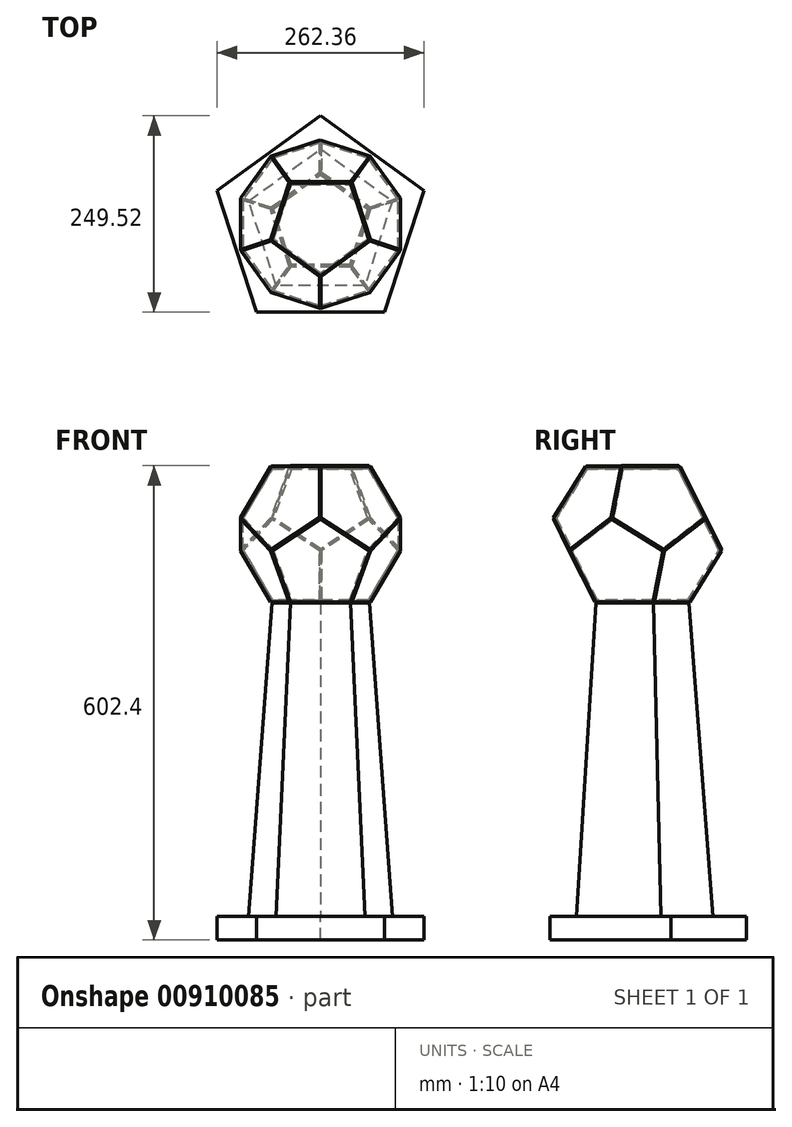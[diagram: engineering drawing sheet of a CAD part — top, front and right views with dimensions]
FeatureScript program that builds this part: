
annotation { "Feature Type Name" : "Feature", "Feature Type Description" : "" }
export const myFeature = defineFeature(function(context is Context, id is Id, definition is map)
    precondition{}
    {
        {
            var Q0;
            Q0=qCreatedBy(makeId("Top.planeOp"),FACE);
            var sketch = newSketch(context, id + "F0", { "sketchPlane" : qUnion([Q0])});
            skCircle(sketch, "E0.cCircle", {"center": v(0, 0) * mm, "radius": 52.66 * mm, "construction": true});
            skLineSegment(sketch, "E0.0", {"start": v(61.9, 20.12) * mm, "end": v(38.26, -52.66) * mm});
            skLineSegment(sketch, "E0.1", {"start": v(38.26, -52.66) * mm, "end": v(-38.26, -52.66) * mm});
            skLineSegment(sketch, "E0.2", {"start": v(-38.26, -52.66) * mm, "end": v(-61.9, 20.12) * mm});
            skLineSegment(sketch, "E0.3", {"start": v(-61.9, 20.12) * mm, "end": v(0, 65.1) * mm});
            skLineSegment(sketch, "E0.4", {"start": v(0, 65.1) * mm, "end": v(61.9, 20.12) * mm});
            skPoint(sketch, "E0.0.midPoint", {"position": v(50.09, -16.27) * mm});
            skSolve(sketch);
        }
        {
            var Q0;
            Q0=makeQuery(id+"F0.imprint","IMPRINT",FACE,{"disambiguationData":[TD([[makeQuery(id+"F0.imprint","IMPRINT",EDGE,{"derivedFrom":sQuery(id+"F0.wireOp",EDGE,"E0.0")}),-1.0]])]});
            extrude(context, id + "F1", {"entities" : qUnion([Q0]), "oppositeDirection" : true, "depth" : 2 * mm, "offsetDistance" : 25.4 * mm, "hasSecondDirection" : true, "secondDirectionOppositeDirection" : false, "secondDirectionDepth" : 2 * mm});
        }
        {
            var Q0;
            Q0=qCreatedBy(makeId("Front.planeOp"),FACE);
            var sketch = newSketch(context, id + "F2", { "sketchPlane" : qUnion([Q0])});
            skLineSegment(sketch, "E1", {"start": v(0, 0) * mm, "end": v(0, 106.17) * mm, "construction": true});
            skSolve(sketch);
        }
        {
            var Q0;
            Q0=makeQuery(id+"F1.opExtrude","SWEPT_BODY",BODY,{"disambiguationData":[OSD([sQuery(id+"F0.wireOp",EDGE,"E0.0"),sQuery(id+"F0.wireOp",EDGE,"E0.1"),sQuery(id+"F0.wireOp",EDGE,"E0.2"),sQuery(id+"F0.wireOp",EDGE,"E0.3"),sQuery(id+"F0.wireOp",EDGE,"E0.4")])]});
            transform(context, id + "F3", {"entities" : qUnion([Q0]), "transformType" : TransformType.COPY});
        }
        {
            var Q0;
            Q0=makeQuery(id+"F3.opPattern","COPY",BODY,{"derivedFrom":makeQuery(id+"F1.opExtrude","SWEPT_BODY",BODY,{"disambiguationData":[OSD([sQuery(id+"F0.wireOp",EDGE,"E0.0"),sQuery(id+"F0.wireOp",EDGE,"E0.1"),sQuery(id+"F0.wireOp",EDGE,"E0.2"),sQuery(id+"F0.wireOp",EDGE,"E0.3"),sQuery(id+"F0.wireOp",EDGE,"E0.4")])]}),"instanceName":"1"});
            var Q1;
            Q1=sQuery(id+"F0.wireOp",EDGE,"E0.4");
            transform(context, id + "F4", {"entities" : qUnion([Q0]), "transformType" : TransformType.ROTATION, "transformAxis" : qUnion([Q1]), "angle" : 116.51 * degree, "oppositeDirection" : true, "makeCopy" : false});
        }
        {
            var Q0;
            Q0=makeQuery(id+"F3.opPattern","COPY",BODY,{"derivedFrom":makeQuery(id+"F1.opExtrude","SWEPT_BODY",BODY,{"disambiguationData":[OSD([sQuery(id+"F0.wireOp",EDGE,"E0.0"),sQuery(id+"F0.wireOp",EDGE,"E0.1"),sQuery(id+"F0.wireOp",EDGE,"E0.2"),sQuery(id+"F0.wireOp",EDGE,"E0.3"),sQuery(id+"F0.wireOp",EDGE,"E0.4")])]}),"instanceName":"1"});
            var Q1;
            Q1=sQuery(id+"F2.wireOp",EDGE,"E1");
            circularPattern(context, id + "F5", {"entities" : qUnion([Q0]), "axis" : qUnion([Q1]), "angle" : 360 * degree, "instanceCount" : 5, "equalSpace" : true});
        }
        {
            var Q0;
            Q0=makeQuery(id+"F3.opPattern","COPY",FACE,{"derivedFrom":makeQuery(id+"F1.opExtrude","SWEPT_FACE",FACE,{"disambiguationData":[OSD([sQuery(id+"F0.wireOp",EDGE,"E0.1")])]}),"instanceName":"1"});
            var sketch = newSketch(context, id + "F6", { "sketchPlane" : qUnion([Q0])});
            skLineSegment(sketch, "E2", {"start": v(-23.08, 92.64) * mm, "end": v(29.66, 37.2) * mm, "construction": true});
            skSolve(sketch);
        }
        {
            var Q0;
            Q0=makeQuery(id+"F3.opPattern","COPY",BODY,{"derivedFrom":makeQuery(id+"F1.opExtrude","SWEPT_BODY",BODY,{"disambiguationData":[OSD([sQuery(id+"F0.wireOp",EDGE,"E0.0"),sQuery(id+"F0.wireOp",EDGE,"E0.1"),sQuery(id+"F0.wireOp",EDGE,"E0.2"),sQuery(id+"F0.wireOp",EDGE,"E0.3"),sQuery(id+"F0.wireOp",EDGE,"E0.4")])]}),"instanceName":"1"});
            transform(context, id + "F7", {"entities" : qUnion([Q0]), "transformType" : TransformType.COPY});
        }
        {
            var Q0;
            Q0=makeQuery(id+"F7.opPattern","COPY",BODY,{"derivedFrom":makeQuery(id+"F3.opPattern","COPY",BODY,{"derivedFrom":makeQuery(id+"F1.opExtrude","SWEPT_BODY",BODY,{"disambiguationData":[OSD([sQuery(id+"F0.wireOp",EDGE,"E0.0"),sQuery(id+"F0.wireOp",EDGE,"E0.1"),sQuery(id+"F0.wireOp",EDGE,"E0.2"),sQuery(id+"F0.wireOp",EDGE,"E0.3"),sQuery(id+"F0.wireOp",EDGE,"E0.4")])]}),"instanceName":"1"}),"instanceName":"1"});
            var Q1;
            Q1=sQuery(id+"F6.wireOp",EDGE,"E2");
            transform(context, id + "F8", {"entities" : qUnion([Q0]), "transformType" : TransformType.ROTATION, "transformAxis" : qUnion([Q1]), "angle" : 116.51 * degree, "oppositeDirection" : true, "makeCopy" : false});
        }
        {
            var Q0;
            Q0=makeQuery(id+"F7.opPattern","COPY",BODY,{"derivedFrom":makeQuery(id+"F3.opPattern","COPY",BODY,{"derivedFrom":makeQuery(id+"F1.opExtrude","SWEPT_BODY",BODY,{"disambiguationData":[OSD([sQuery(id+"F0.wireOp",EDGE,"E0.0"),sQuery(id+"F0.wireOp",EDGE,"E0.1"),sQuery(id+"F0.wireOp",EDGE,"E0.2"),sQuery(id+"F0.wireOp",EDGE,"E0.3"),sQuery(id+"F0.wireOp",EDGE,"E0.4")])]}),"instanceName":"1"}),"instanceName":"1"});
            var Q1;
            Q1=sQuery(id+"F2.wireOp",EDGE,"E1");
            circularPattern(context, id + "F9", {"entities" : qUnion([Q0]), "axis" : qUnion([Q1]), "angle" : 360 * degree, "instanceCount" : 5, "equalSpace" : true});
        }
        {
            var Q0;
            Q0=makeQuery(id+"F7.opPattern","COPY",FACE,{"derivedFrom":makeQuery(id+"F3.opPattern","COPY",FACE,{"derivedFrom":makeQuery(id+"F1.opExtrude","SWEPT_FACE",FACE,{"disambiguationData":[OSD([sQuery(id+"F0.wireOp",EDGE,"E0.3")])]}),"instanceName":"1"}),"instanceName":"1"});
            var sketch = newSketch(context, id + "F10", { "sketchPlane" : qUnion([Q0])});
            skLineSegment(sketch, "E3", {"start": v(102.83, 78.1) * mm, "end": v(128.69, 6.84) * mm, "construction": true});
            skSolve(sketch);
        }
        {
            var Q0;
            Q0=makeQuery(id+"F9.opPattern","COPY",BODY,{"derivedFrom":makeQuery(id+"F7.opPattern","COPY",BODY,{"derivedFrom":makeQuery(id+"F3.opPattern","COPY",BODY,{"derivedFrom":makeQuery(id+"F1.opExtrude","SWEPT_BODY",BODY,{"disambiguationData":[OSD([sQuery(id+"F0.wireOp",EDGE,"E0.0"),sQuery(id+"F0.wireOp",EDGE,"E0.1"),sQuery(id+"F0.wireOp",EDGE,"E0.2"),sQuery(id+"F0.wireOp",EDGE,"E0.3"),sQuery(id+"F0.wireOp",EDGE,"E0.4")])]}),"instanceName":"1"}),"instanceName":"1"}),"instanceName":"4"});
            transform(context, id + "F11", {"entities" : qUnion([Q0]), "transformType" : TransformType.COPY});
        }
        {
            var Q0;
            Q0=makeQuery(id+"F7.opPattern","COPY",BODY,{"derivedFrom":makeQuery(id+"F3.opPattern","COPY",BODY,{"derivedFrom":makeQuery(id+"F1.opExtrude","SWEPT_BODY",BODY,{"disambiguationData":[OSD([sQuery(id+"F0.wireOp",EDGE,"E0.0"),sQuery(id+"F0.wireOp",EDGE,"E0.1"),sQuery(id+"F0.wireOp",EDGE,"E0.2"),sQuery(id+"F0.wireOp",EDGE,"E0.3"),sQuery(id+"F0.wireOp",EDGE,"E0.4")])]}),"instanceName":"1"}),"instanceName":"1"});
            transform(context, id + "F12", {"entities" : qUnion([Q0]), "transformType" : TransformType.COPY});
        }
        {
            var Q0;
            Q0=makeQuery(id+"F11.opPattern","COPY",BODY,{"derivedFrom":makeQuery(id+"F9.opPattern","COPY",BODY,{"derivedFrom":makeQuery(id+"F7.opPattern","COPY",BODY,{"derivedFrom":makeQuery(id+"F3.opPattern","COPY",BODY,{"derivedFrom":makeQuery(id+"F1.opExtrude","SWEPT_BODY",BODY,{"disambiguationData":[OSD([sQuery(id+"F0.wireOp",EDGE,"E0.0"),sQuery(id+"F0.wireOp",EDGE,"E0.1"),sQuery(id+"F0.wireOp",EDGE,"E0.2"),sQuery(id+"F0.wireOp",EDGE,"E0.3"),sQuery(id+"F0.wireOp",EDGE,"E0.4")])]}),"instanceName":"1"}),"instanceName":"1"}),"instanceName":"4"}),"instanceName":"1"});
            deleteBodies(context, id + "F13", {"entities" : qUnion([Q0])});
        }
        {
            var Q0;
            Q0=makeQuery(id+"F12.opPattern","COPY",BODY,{"derivedFrom":makeQuery(id+"F7.opPattern","COPY",BODY,{"derivedFrom":makeQuery(id+"F3.opPattern","COPY",BODY,{"derivedFrom":makeQuery(id+"F1.opExtrude","SWEPT_BODY",BODY,{"disambiguationData":[OSD([sQuery(id+"F0.wireOp",EDGE,"E0.0"),sQuery(id+"F0.wireOp",EDGE,"E0.1"),sQuery(id+"F0.wireOp",EDGE,"E0.2"),sQuery(id+"F0.wireOp",EDGE,"E0.3"),sQuery(id+"F0.wireOp",EDGE,"E0.4")])]}),"instanceName":"1"}),"instanceName":"1"}),"instanceName":"1"});
            var Q1;
            Q1=sQuery(id+"F10.wireOp",EDGE,"E3");
            transform(context, id + "F14", {"entities" : qUnion([Q0]), "transformType" : TransformType.ROTATION, "transformAxis" : qUnion([Q1]), "angle" : 116.51 * degree, "oppositeDirection" : true, "makeCopy" : false});
        }
        {
            var Q0;
            Q0=makeQuery(id+"F1.opExtrude","CAP_FACE",FACE,{"disambiguationData":[OSD([sQuery(id+"F0.wireOp",EDGE,"E0.0"),sQuery(id+"F0.wireOp",EDGE,"E0.1"),sQuery(id+"F0.wireOp",EDGE,"E0.2"),sQuery(id+"F0.wireOp",EDGE,"E0.3"),sQuery(id+"F0.wireOp",EDGE,"E0.4")])],"isStart":false});
            var sketch = newSketch(context, id + "F15", { "sketchPlane" : qUnion([Q0])});
            skCircle(sketch, "E4.cCircle", {"center": v(0, 0) * mm, "radius": 52.66 * mm, "construction": true});
            skLineSegment(sketch, "E4.0", {"start": v(38.26, 52.66) * mm, "end": v(61.9, -20.12) * mm});
            skLineSegment(sketch, "E4.1", {"start": v(61.9, -20.12) * mm, "end": v(0, -65.1) * mm});
            skLineSegment(sketch, "E4.2", {"start": v(0, -65.1) * mm, "end": v(-61.9, -20.12) * mm});
            skLineSegment(sketch, "E4.3", {"start": v(-61.9, -20.12) * mm, "end": v(-38.26, 52.66) * mm});
            skLineSegment(sketch, "E4.4", {"start": v(-38.26, 52.66) * mm, "end": v(38.26, 52.66) * mm});
            skPoint(sketch, "E4.0.midPoint", {"position": v(50.09, 16.27) * mm});
            skPoint(sketch, "E5.0.midPoint", {"position": v(36.93, 12) * mm});
            skPoint(sketch, "E6.orphan", {"position": v(28.22, 38.83) * mm});
            skPoint(sketch, "E7.orphan", {"position": v(45.65, -14.83) * mm});
            skSolve(sketch);
        }
        {
            var Q0;
            Q0=qCreatedBy(makeId("Top.planeOp"),FACE);
            cPlane(context, id + "F16", {"entities" : qUnion([Q0]), "cplaneType" : CPlaneType.OFFSET, "offset" : 400 * mm, "oppositeDirection" : true, "width" : 150 * mm, "height" : 150 * mm});
        }
        {
            var Q0;
            Q0=qCreatedBy(id+"F16.planeOp",FACE);
            var sketch = newSketch(context, id + "F17", { "sketchPlane" : qUnion([Q0])});
            skCircle(sketch, "E8.cCircle", {"center": v(0, 0) * mm, "radius": 77.57 * mm, "construction": true});
            skLineSegment(sketch, "E8.0", {"start": v(56.36, -77.57) * mm, "end": v(-56.36, -77.57) * mm});
            skLineSegment(sketch, "E8.1", {"start": v(-56.36, -77.57) * mm, "end": v(-91.2, 29.63) * mm});
            skLineSegment(sketch, "E8.2", {"start": v(-91.2, 29.63) * mm, "end": v(0, 95.88) * mm});
            skLineSegment(sketch, "E8.3", {"start": v(0, 95.88) * mm, "end": v(91.2, 29.63) * mm});
            skLineSegment(sketch, "E8.4", {"start": v(91.2, 29.63) * mm, "end": v(56.36, -77.57) * mm});
            skPoint(sketch, "E8.0.midPoint", {"position": v(0, -77.57) * mm});
            skSolve(sketch);
        }
        {
            var Q1;
            Q1=makeQuery(id+"F15.imprint","IMPRINT",FACE,{"disambiguationData":[TD([[makeQuery(id+"F15.imprint","IMPRINT",EDGE,{"derivedFrom":sQuery(id+"F15.wireOp",EDGE,"E4.0")}),1.0]])]});
            var Q2;
            Q2=makeQuery(id+"F17.imprint","IMPRINT",FACE,{"disambiguationData":[TD([[makeQuery(id+"F17.imprint","IMPRINT",EDGE,{"derivedFrom":sQuery(id+"F17.wireOp",EDGE,"E8.0")}),-1.0]])]});
            loft(context, id + "F18", {"operationType" : NewBodyOperationType.ADD, "sheetProfilesArray" : [{ "sheetProfileEntities" : qUnion([Q1]) }, { "sheetProfileEntities" : qUnion([Q2]) }]});
        }
        {
            var Q0;
            Q0=qCreatedBy(id+"F16.planeOp",FACE);
            var sketch = newSketch(context, id + "F19", { "sketchPlane" : qUnion([Q0])});
            skCircle(sketch, "E9.cCircle", {"center": v(0, 0) * mm, "radius": 111.59 * mm, "construction": true});
            skLineSegment(sketch, "E9.0", {"start": v(81.07, -111.59) * mm, "end": v(-81.07, -111.59) * mm});
            skLineSegment(sketch, "E9.1", {"start": v(-81.07, -111.59) * mm, "end": v(-131.18, 42.62) * mm});
            skLineSegment(sketch, "E9.2", {"start": v(-131.18, 42.62) * mm, "end": v(0, 137.93) * mm});
            skLineSegment(sketch, "E9.3", {"start": v(0, 137.93) * mm, "end": v(131.18, 42.62) * mm});
            skLineSegment(sketch, "E9.4", {"start": v(131.18, 42.62) * mm, "end": v(81.07, -111.59) * mm});
            skPoint(sketch, "E9.0.midPoint", {"position": v(0, -111.59) * mm});
            skSolve(sketch);
        }
        {
            var Q0;
            Q0 = qSketchRegion(id + "F19", true);
            extrude(context, id + "F20", {"entities" : qUnion([Q0]), "operationType" : NewBodyOperationType.ADD, "oppositeDirection" : true, "depth" : 30 * mm, "offsetDistance" : 25 * mm});
        }
    });
